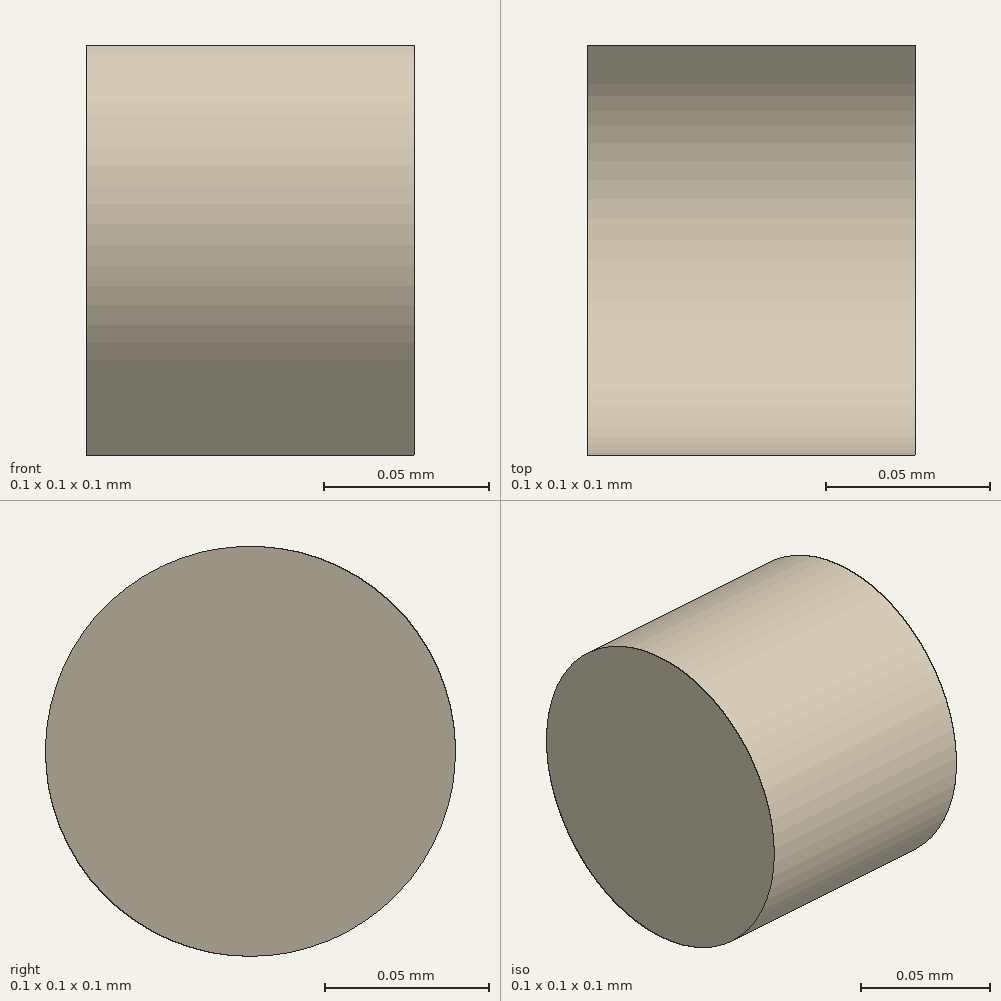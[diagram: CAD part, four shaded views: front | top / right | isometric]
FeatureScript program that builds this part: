
annotation { "Feature Type Name" : "Feature", "Feature Type Description" : "" }
export const myFeature = defineFeature(function(context is Context, id is Id, definition is map)
    precondition{}
    {
        {
            var Q0;
            Q0=qCreatedBy(makeId("Right.planeOp"),FACE);
            var sketch = newSketch(context, id + "F0", { "sketchPlane" : qUnion([Q0])});
            skCircle(sketch, "E0", {"center": v(0, 0) * mm, "radius": 0.06 * mm});
            skSolve(sketch);
        }
        {
            var Q0;
            Q0=qSketchRegion(id+"F0",true);
            extrude(context, id + "F1", {"entities" : qUnion([Q0]), "depth" : 0.1 * mm, "offsetDistance" : 25 * mm});
        }
    });
